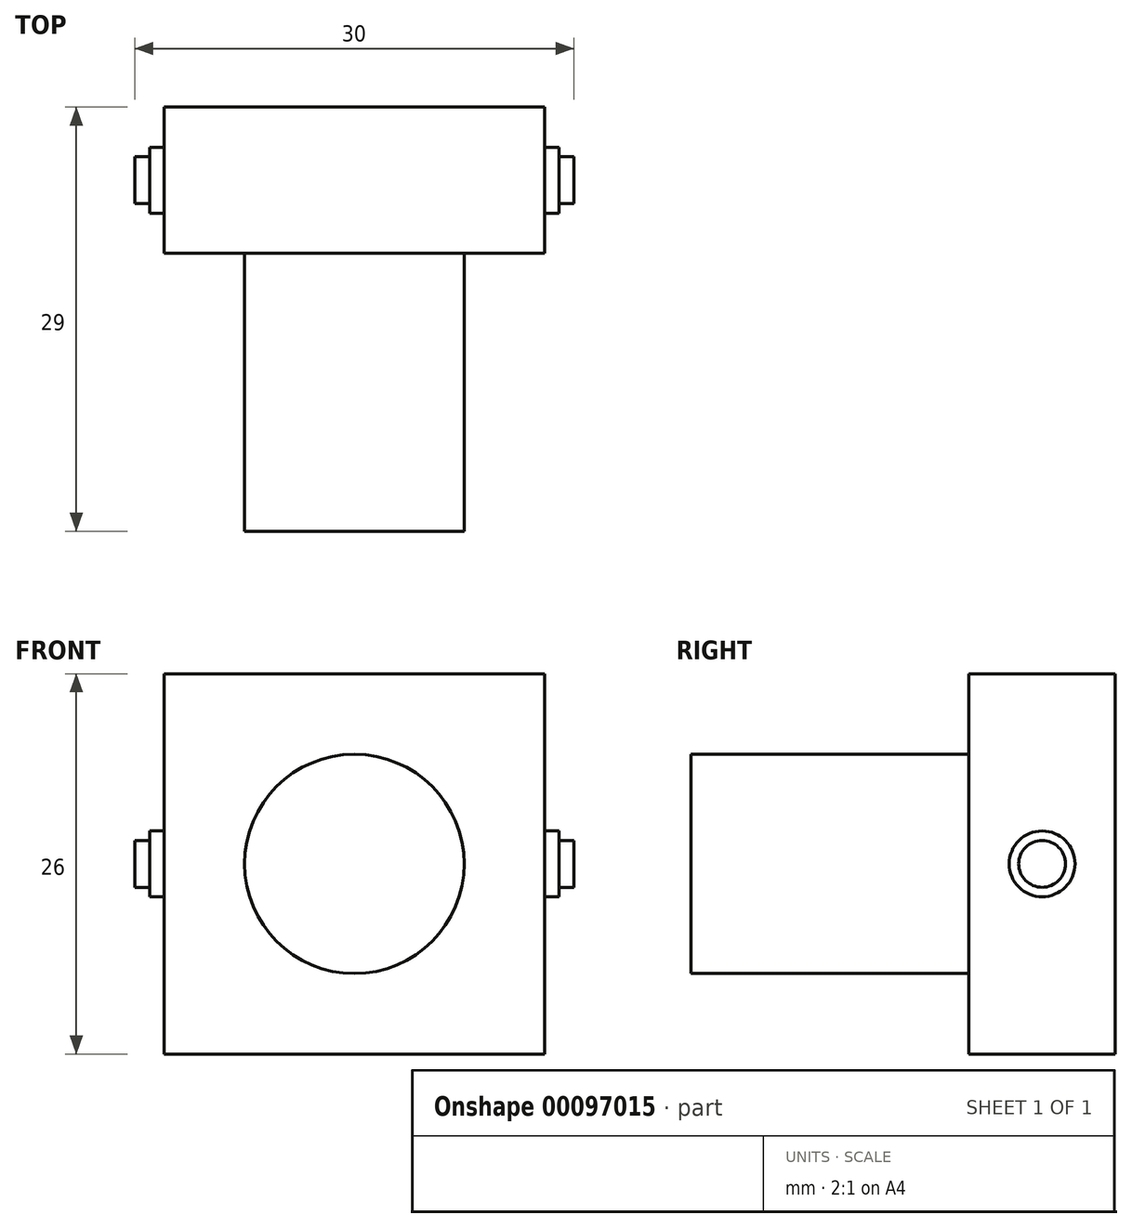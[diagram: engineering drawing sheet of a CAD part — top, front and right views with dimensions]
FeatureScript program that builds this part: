
annotation { "Feature Type Name" : "Feature", "Feature Type Description" : "" }
export const myFeature = defineFeature(function(context is Context, id is Id, definition is map)
    precondition{}
    {
        {
            var Q0;
            Q0=qCreatedBy(makeId("Front.planeOp"),FACE);
            var sketch = newSketch(context, id + "F0", { "sketchPlane" : qUnion([Q0])});
            skLineSegment(sketch, "E0.bottom", {"start": v(-13, 13) * mm, "end": v(13, 13) * mm});
            skLineSegment(sketch, "E0.top", {"start": v(-13, -13) * mm, "end": v(13, -13) * mm});
            skLineSegment(sketch, "E0.left", {"start": v(-13, 13) * mm, "end": v(-13, -13) * mm});
            skLineSegment(sketch, "E0.right", {"start": v(13, 13) * mm, "end": v(13, -13) * mm});
            skPoint(sketch, "E0.middle", {"position": v(0, 0) * mm});
            skSolve(sketch);
        }
        {
            var Q0;
            Q0=makeQuery(id+"F0.imprint","IMPRINT",FACE,{"disambiguationData":[TD([[makeQuery(id+"F0.imprint","IMPRINT",EDGE,{"derivedFrom":sQuery(id+"F0.wireOp",EDGE,"E0.bottom")}),-1.0]])]});
            extrude(context, id + "F1", {"entities" : qUnion([Q0]), "depth" : 10 * mm});
        }
        {
            var Q0;
            Q0=makeQuery(id+"F1.opExtrude","CAP_FACE",FACE,{"disambiguationData":[OSD([sQuery(id+"F0.wireOp",EDGE,"E0.bottom"),sQuery(id+"F0.wireOp",EDGE,"E0.top"),sQuery(id+"F0.wireOp",EDGE,"E0.left"),sQuery(id+"F0.wireOp",EDGE,"E0.right")])],"isStart":false});
            var sketch = newSketch(context, id + "F2", { "sketchPlane" : qUnion([Q0])});
            skCircle(sketch, "E1", {"center": v(0, 0) * mm, "radius": 7.5 * mm});
            skSolve(sketch);
        }
        {
            var Q0;
            Q0 = qSketchRegion(id + "F2", true);
            extrude(context, id + "F3", {"entities" : qUnion([Q0]), "operationType" : NewBodyOperationType.ADD, "depth" : 19 * mm});
        }
        {
            var Q0;
            Q0=makeQuery(id+"F1.opExtrude","SWEPT_FACE",FACE,{"disambiguationData":[OSD([sQuery(id+"F0.wireOp",EDGE,"E0.right")])]});
            var sketch = newSketch(context, id + "F4", { "sketchPlane" : qUnion([Q0])});
            skLineSegment(sketch, "E2", {"start": v(-10, 0) * mm, "end": v(0, 0) * mm});
            skPoint(sketch, "E3", {"position": v(-5, 0) * mm});
            skCircle(sketch, "E4", {"center": v(-5, 0) * mm, "radius": 2.25 * mm});
            skSolve(sketch);
        }
        {
            var Q0;
            Q0 = qSketchRegion(id + "F4", true);
            extrude(context, id + "F5", {"entities" : qUnion([Q0]), "operationType" : NewBodyOperationType.ADD, "depth" : 1 * mm});
        }
        {
            var Q0;
            Q0=makeQuery(id+"F1.opExtrude","SWEPT_FACE",FACE,{"disambiguationData":[OSD([sQuery(id+"F0.wireOp",EDGE,"E0.left")])]});
            var sketch = newSketch(context, id + "F6", { "sketchPlane" : qUnion([Q0])});
            skLineSegment(sketch, "E5", {"start": v(0, 0) * mm, "end": v(10, 0) * mm});
            skPoint(sketch, "E6", {"position": v(5, 0) * mm});
            skCircle(sketch, "E7", {"center": v(5, 0) * mm, "radius": 2.25 * mm});
            skSolve(sketch);
        }
        {
            var Q0;
            Q0 = qSketchRegion(id + "F6", true);
            extrude(context, id + "F7", {"entities" : qUnion([Q0]), "operationType" : NewBodyOperationType.ADD, "depth" : 1 * mm});
        }
        {
            var Q0;
            Q0=makeQuery(id+"F7.opExtrude","CAP_FACE",FACE,{"disambiguationData":[OSD([sQuery(id+"F6.wireOp",EDGE,"E7")])],"isStart":false});
            var sketch = newSketch(context, id + "F8", { "sketchPlane" : qUnion([Q0])});
            skCircle(sketch, "E8", {"center": v(5, 0) * mm, "radius": 1.6 * mm});
            skSolve(sketch);
        }
        {
            var Q0;
            Q0 = qSketchRegion(id + "F8", true);
            extrude(context, id + "F9", {"entities" : qUnion([Q0]), "operationType" : NewBodyOperationType.ADD, "depth" : 1 * mm});
        }
        {
            var Q0;
            Q0=makeQuery(id+"F5.opExtrude","CAP_FACE",FACE,{"disambiguationData":[OSD([sQuery(id+"F4.wireOp",EDGE,"E4")])],"isStart":false});
            var sketch = newSketch(context, id + "F10", { "sketchPlane" : qUnion([Q0])});
            skCircle(sketch, "E9", {"center": v(-5, 0) * mm, "radius": 1.6 * mm});
            skSolve(sketch);
        }
        {
            var Q0;
            Q0=makeQuery(id+"F10.imprint","IMPRINT",FACE,{"disambiguationData":[TD([[makeQuery(id+"F10.imprint","IMPRINT",EDGE,{"derivedFrom":sQuery(id+"F10.wireOp",EDGE,"E9")}),1.0]])]});
            extrude(context, id + "F11", {"entities" : qUnion([Q0]), "operationType" : NewBodyOperationType.ADD, "depth" : 1 * mm});
        }
    });
